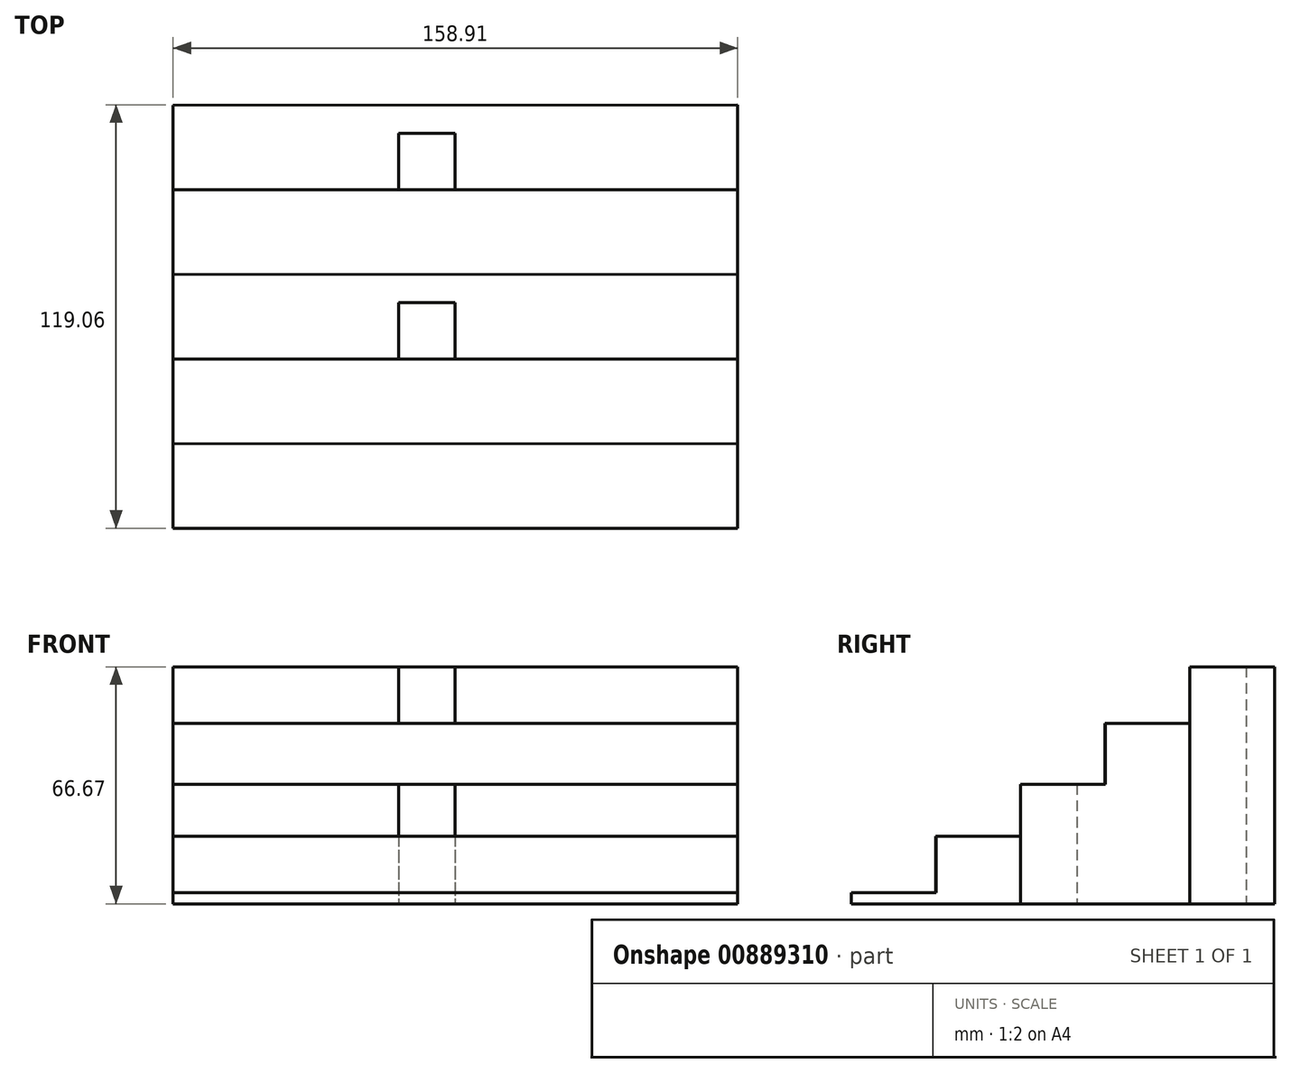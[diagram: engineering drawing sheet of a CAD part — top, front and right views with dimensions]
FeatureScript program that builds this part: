
annotation { "Feature Type Name" : "Feature", "Feature Type Description" : "" }
export const myFeature = defineFeature(function(context is Context, id is Id, definition is map)
    precondition{}
    {
        {
            var Q0;
            Q0=qCreatedBy(makeId("Top.planeOp"),FACE);
            var sketch = newSketch(context, id + "F0", { "sketchPlane" : qUnion([Q0])});
            skLineSegment(sketch, "E0", {"start": v(0, 0) * mm, "end": v(15.88, 0) * mm});
            skLineSegment(sketch, "E1", {"start": v(15.88, 0) * mm, "end": v(15.88, 15.88) * mm});
            skLineSegment(sketch, "E2", {"start": v(15.88, 15.88) * mm, "end": v(0, 15.88) * mm});
            skLineSegment(sketch, "E3", {"start": v(0, 15.88) * mm, "end": v(0, 0) * mm});
            skLineSegment(sketch, "E4.1.0.0", {"start": v(31.75, 0) * mm, "end": v(47.62, 0) * mm});
            skLineSegment(sketch, "E4.1.0.1", {"start": v(31.75, 15.88) * mm, "end": v(31.75, 0) * mm});
            skLineSegment(sketch, "E4.1.0.2", {"start": v(47.62, 0) * mm, "end": v(47.62, 15.88) * mm});
            skLineSegment(sketch, "E4.1.0.3", {"start": v(47.62, 15.88) * mm, "end": v(31.75, 15.88) * mm});
            skLineSegment(sketch, "E4.2.0.0", {"start": v(63.5, 0) * mm, "end": v(79.38, 0) * mm});
            skLineSegment(sketch, "E4.2.0.1", {"start": v(63.5, 15.88) * mm, "end": v(63.5, 0) * mm});
            skLineSegment(sketch, "E4.2.0.2", {"start": v(79.38, 0) * mm, "end": v(79.38, 15.88) * mm});
            skLineSegment(sketch, "E4.2.0.3", {"start": v(79.38, 15.88) * mm, "end": v(63.5, 15.88) * mm});
            skLineSegment(sketch, "E4.3.0.0", {"start": v(95.25, 0) * mm, "end": v(111.12, 0) * mm});
            skLineSegment(sketch, "E4.3.0.1", {"start": v(95.25, 15.88) * mm, "end": v(95.25, 0) * mm});
            skLineSegment(sketch, "E4.3.0.2", {"start": v(111.12, 0) * mm, "end": v(111.12, 15.88) * mm});
            skLineSegment(sketch, "E4.3.0.3", {"start": v(111.12, 15.88) * mm, "end": v(95.25, 15.88) * mm});
            skLineSegment(sketch, "E4.4.0.0", {"start": v(127, 0) * mm, "end": v(142.88, 0) * mm});
            skLineSegment(sketch, "E4.4.0.1", {"start": v(127, 15.88) * mm, "end": v(127, 0) * mm});
            skLineSegment(sketch, "E4.4.0.2", {"start": v(142.88, 0) * mm, "end": v(142.88, 15.88) * mm});
            skLineSegment(sketch, "E4.4.0.3", {"start": v(142.88, 15.88) * mm, "end": v(127, 15.88) * mm});
            skLineSegment(sketch, "E4.direction1", {"start": v(0, 0) * mm, "end": v(31.75, 0) * mm, "construction": true});
            skLineSegment(sketch, "E5.direction1", {"start": v(0, 0) * mm, "end": v(25.4, 0) * mm, "construction": true});
            skLineSegment(sketch, "E5.direction2", {"start": v(0, 0) * mm, "end": v(0, 0) * mm});
            skLineSegment(sketch, "E6.direction1", {"start": v(15.88, 0) * mm, "end": v(31.75, 0) * mm, "construction": true});
            skLineSegment(sketch, "E7", {"start": v(15.88, 23.81) * mm, "end": v(15.88, 39.69) * mm});
            skLineSegment(sketch, "E8", {"start": v(15.88, 39.69) * mm, "end": v(31.8, 39.69) * mm});
            skLineSegment(sketch, "E9", {"start": v(31.8, 39.69) * mm, "end": v(31.8, 23.81) * mm});
            skLineSegment(sketch, "E10", {"start": v(31.8, 23.81) * mm, "end": v(15.88, 23.81) * mm});
            skLineSegment(sketch, "E11.1.0.0", {"start": v(47.62, 23.81) * mm, "end": v(47.62, 39.69) * mm});
            skLineSegment(sketch, "E11.1.0.1", {"start": v(63.55, 39.69) * mm, "end": v(63.55, 23.81) * mm});
            skLineSegment(sketch, "E11.1.0.2", {"start": v(63.55, 23.81) * mm, "end": v(47.62, 23.81) * mm});
            skLineSegment(sketch, "E11.1.0.3", {"start": v(47.62, 39.69) * mm, "end": v(63.55, 39.69) * mm});
            skLineSegment(sketch, "E11.2.0.0", {"start": v(79.38, 23.81) * mm, "end": v(79.38, 39.69) * mm});
            skLineSegment(sketch, "E11.2.0.1", {"start": v(95.3, 39.69) * mm, "end": v(95.3, 23.81) * mm});
            skLineSegment(sketch, "E11.2.0.2", {"start": v(95.3, 23.81) * mm, "end": v(79.37, 23.81) * mm});
            skLineSegment(sketch, "E11.2.0.3", {"start": v(79.37, 39.69) * mm, "end": v(95.3, 39.69) * mm});
            skLineSegment(sketch, "E11.3.0.0", {"start": v(111.12, 23.81) * mm, "end": v(111.12, 39.69) * mm});
            skLineSegment(sketch, "E11.3.0.1", {"start": v(127.05, 39.69) * mm, "end": v(127.05, 23.81) * mm});
            skLineSegment(sketch, "E11.3.0.2", {"start": v(127.05, 23.81) * mm, "end": v(111.12, 23.81) * mm});
            skLineSegment(sketch, "E11.3.0.3", {"start": v(111.12, 39.69) * mm, "end": v(127.05, 39.69) * mm});
            skLineSegment(sketch, "E11.4.0.0", {"start": v(142.88, 23.81) * mm, "end": v(142.88, 39.69) * mm});
            skLineSegment(sketch, "E11.4.0.1", {"start": v(158.8, 39.69) * mm, "end": v(158.8, 23.81) * mm});
            skLineSegment(sketch, "E11.4.0.2", {"start": v(158.8, 23.81) * mm, "end": v(142.87, 23.81) * mm});
            skLineSegment(sketch, "E11.4.0.3", {"start": v(142.87, 39.69) * mm, "end": v(158.8, 39.69) * mm});
            skLineSegment(sketch, "E11.direction1", {"start": v(15.88, 23.81) * mm, "end": v(47.62, 23.81) * mm, "construction": true});
            skLineSegment(sketch, "E12", {"start": v(158.8, 23.81) * mm, "end": v(158.8, 0) * mm});
            skLineSegment(sketch, "E13", {"start": v(158.8, 0) * mm, "end": v(0, 0) * mm});
            skLineSegment(sketch, "E14", {"start": v(-0.01, 23.74) * mm, "end": v(158.8, 23.81) * mm});
            skLineSegment(sketch, "E15", {"start": v(-0.01, 23.74) * mm, "end": v(0, 0) * mm});
            skLineSegment(sketch, "E16", {"start": v(-0.01, 23.74) * mm, "end": v(-0.02, 47.62) * mm});
            skLineSegment(sketch, "E17", {"start": v(-0.02, 47.62) * mm, "end": v(158.89, 47.62) * mm});
            skLineSegment(sketch, "E18", {"start": v(158.89, 47.62) * mm, "end": v(158.8, 23.81) * mm});
            skLineSegment(sketch, "E19.0.1.0", {"start": v(142.88, 71.44) * mm, "end": v(142.88, 87.31) * mm});
            skLineSegment(sketch, "E19.0.1.1", {"start": v(142.88, 47.63) * mm, "end": v(142.88, 63.5) * mm});
            skLineSegment(sketch, "E19.0.1.2", {"start": v(-0.01, 71.37) * mm, "end": v(158.8, 71.44) * mm});
            skLineSegment(sketch, "E19.0.1.3", {"start": v(79.37, 87.31) * mm, "end": v(95.3, 87.31) * mm});
            skLineSegment(sketch, "E19.0.1.4", {"start": v(158.8, 47.63) * mm, "end": v(0, 47.63) * mm});
            skLineSegment(sketch, "E19.0.1.5", {"start": v(15.88, 63.5) * mm, "end": v(0, 63.5) * mm});
            skLineSegment(sketch, "E19.0.1.6", {"start": v(127, 63.5) * mm, "end": v(127, 47.63) * mm});
            skLineSegment(sketch, "E19.0.1.7", {"start": v(63.5, 47.63) * mm, "end": v(79.38, 47.63) * mm});
            skLineSegment(sketch, "E19.0.1.8", {"start": v(15.88, 47.63) * mm, "end": v(15.88, 63.5) * mm});
            skLineSegment(sketch, "E19.0.1.9", {"start": v(111.12, 63.5) * mm, "end": v(95.25, 63.5) * mm});
            skLineSegment(sketch, "E19.0.1.10", {"start": v(0, 63.5) * mm, "end": v(0, 47.63) * mm});
            skLineSegment(sketch, "E19.0.1.11", {"start": v(15.88, 71.44) * mm, "end": v(15.88, 87.31) * mm});
            skLineSegment(sketch, "E19.0.1.12", {"start": v(158.8, 71.44) * mm, "end": v(142.87, 71.44) * mm});
            skLineSegment(sketch, "E19.0.1.13", {"start": v(-0.01, 71.37) * mm, "end": v(0, 47.63) * mm});
            skLineSegment(sketch, "E19.0.1.14", {"start": v(47.62, 87.31) * mm, "end": v(63.55, 87.31) * mm});
            skLineSegment(sketch, "E19.0.1.15", {"start": v(47.62, 71.44) * mm, "end": v(47.62, 87.31) * mm});
            skLineSegment(sketch, "E19.0.1.16", {"start": v(142.87, 87.31) * mm, "end": v(158.8, 87.31) * mm});
            skLineSegment(sketch, "E19.0.1.17", {"start": v(47.62, 47.63) * mm, "end": v(47.62, 63.5) * mm});
            skLineSegment(sketch, "E19.0.1.18", {"start": v(63.55, 87.31) * mm, "end": v(63.55, 71.44) * mm});
            skLineSegment(sketch, "E19.0.1.19", {"start": v(79.38, 63.5) * mm, "end": v(63.5, 63.5) * mm});
            skLineSegment(sketch, "E19.0.1.20", {"start": v(79.38, 71.44) * mm, "end": v(79.38, 87.31) * mm});
            skLineSegment(sketch, "E19.0.1.21", {"start": v(79.38, 47.63) * mm, "end": v(79.38, 63.5) * mm});
            skLineSegment(sketch, "E19.0.1.22", {"start": v(15.88, 87.31) * mm, "end": v(31.8, 87.31) * mm});
            skLineSegment(sketch, "E19.0.1.23", {"start": v(142.88, 63.5) * mm, "end": v(127, 63.5) * mm});
            skLineSegment(sketch, "E19.0.1.24", {"start": v(-0.02, 95.25) * mm, "end": v(158.89, 95.25) * mm});
            skLineSegment(sketch, "E19.0.1.25", {"start": v(95.25, 47.63) * mm, "end": v(111.12, 47.63) * mm});
            skLineSegment(sketch, "E19.0.1.26", {"start": v(31.75, 63.5) * mm, "end": v(31.75, 47.63) * mm});
            skLineSegment(sketch, "E19.0.1.27", {"start": v(111.12, 87.31) * mm, "end": v(127.05, 87.31) * mm});
            skLineSegment(sketch, "E19.0.1.28", {"start": v(127, 47.63) * mm, "end": v(142.88, 47.63) * mm});
            skLineSegment(sketch, "E19.0.1.29", {"start": v(63.5, 63.5) * mm, "end": v(63.5, 47.63) * mm});
            skLineSegment(sketch, "E19.0.1.30", {"start": v(95.25, 63.5) * mm, "end": v(95.25, 47.63) * mm});
            skLineSegment(sketch, "E19.0.1.31", {"start": v(127.05, 71.44) * mm, "end": v(111.12, 71.44) * mm});
            skLineSegment(sketch, "E19.0.1.32", {"start": v(63.55, 71.44) * mm, "end": v(47.62, 71.44) * mm});
            skLineSegment(sketch, "E19.0.1.33", {"start": v(47.62, 63.5) * mm, "end": v(31.75, 63.5) * mm});
            skLineSegment(sketch, "E19.0.1.34", {"start": v(111.12, 71.44) * mm, "end": v(111.12, 87.31) * mm});
            skLineSegment(sketch, "E19.0.1.35", {"start": v(95.3, 71.44) * mm, "end": v(79.37, 71.44) * mm});
            skLineSegment(sketch, "E19.0.1.36", {"start": v(31.8, 87.31) * mm, "end": v(31.8, 71.44) * mm});
            skLineSegment(sketch, "E19.0.1.37", {"start": v(111.12, 47.63) * mm, "end": v(111.12, 63.5) * mm});
            skLineSegment(sketch, "E19.0.1.38", {"start": v(31.8, 71.44) * mm, "end": v(15.88, 71.44) * mm});
            skLineSegment(sketch, "E19.0.1.39", {"start": v(127.05, 87.31) * mm, "end": v(127.05, 71.44) * mm});
            skLineSegment(sketch, "E19.0.1.40", {"start": v(-0.01, 71.37) * mm, "end": v(-0.02, 95.25) * mm});
            skLineSegment(sketch, "E19.0.1.41", {"start": v(95.3, 87.31) * mm, "end": v(95.3, 71.44) * mm});
            skLineSegment(sketch, "E19.0.1.42", {"start": v(158.89, 95.25) * mm, "end": v(158.8, 71.44) * mm});
            skLineSegment(sketch, "E19.0.1.43", {"start": v(158.8, 71.44) * mm, "end": v(158.8, 47.63) * mm});
            skLineSegment(sketch, "E19.0.1.44", {"start": v(0, 47.63) * mm, "end": v(15.88, 47.63) * mm});
            skLineSegment(sketch, "E19.0.1.45", {"start": v(15.88, 71.44) * mm, "end": v(47.62, 71.44) * mm, "construction": true});
            skLineSegment(sketch, "E19.0.1.46", {"start": v(0, 47.63) * mm, "end": v(25.4, 47.63) * mm, "construction": true});
            skLineSegment(sketch, "E19.0.1.47", {"start": v(0, 47.63) * mm, "end": v(31.75, 47.63) * mm, "construction": true});
            skLineSegment(sketch, "E19.0.1.48", {"start": v(158.8, 87.31) * mm, "end": v(158.8, 71.44) * mm});
            skLineSegment(sketch, "E19.0.1.49", {"start": v(31.75, 47.63) * mm, "end": v(47.62, 47.63) * mm});
            skLineSegment(sketch, "E19.0.1.50", {"start": v(15.88, 47.63) * mm, "end": v(31.75, 47.63) * mm, "construction": true});
            skLineSegment(sketch, "E19.direction2", {"start": v(0, 0) * mm, "end": v(0, 47.63) * mm, "construction": true});
            skLineSegment(sketch, "E20.3.0.2", {"start": v(142.88, 95.25) * mm, "end": v(142.88, 111.12) * mm});
            skLineSegment(sketch, "E20.6.0.2", {"start": v(-0.01, 119) * mm, "end": v(158.8, 119.06) * mm});
            skLineSegment(sketch, "E20.12.0.2", {"start": v(158.8, 95.25) * mm, "end": v(0, 95.25) * mm});
            skLineSegment(sketch, "E20.15.0.2", {"start": v(15.88, 111.12) * mm, "end": v(0, 111.12) * mm});
            skLineSegment(sketch, "E20.18.0.2", {"start": v(127, 111.12) * mm, "end": v(127, 95.25) * mm});
            skLineSegment(sketch, "E20.21.0.2", {"start": v(63.5, 95.25) * mm, "end": v(79.38, 95.25) * mm});
            skLineSegment(sketch, "E20.24.0.2", {"start": v(15.88, 95.25) * mm, "end": v(15.88, 111.12) * mm});
            skLineSegment(sketch, "E20.27.0.2", {"start": v(111.12, 111.12) * mm, "end": v(95.25, 111.12) * mm});
            skLineSegment(sketch, "E20.30.0.2", {"start": v(0, 111.12) * mm, "end": v(0, 95.25) * mm});
            skLineSegment(sketch, "E20.39.0.2", {"start": v(-0.01, 119) * mm, "end": v(0, 95.25) * mm});
            skLineSegment(sketch, "E20.51.0.2", {"start": v(47.62, 95.25) * mm, "end": v(47.62, 111.12) * mm});
            skLineSegment(sketch, "E20.57.0.2", {"start": v(79.38, 111.12) * mm, "end": v(63.5, 111.12) * mm});
            skLineSegment(sketch, "E20.63.0.2", {"start": v(79.38, 95.25) * mm, "end": v(79.38, 111.12) * mm});
            skLineSegment(sketch, "E20.69.0.2", {"start": v(142.88, 111.12) * mm, "end": v(127, 111.12) * mm});
            skLineSegment(sketch, "E20.75.0.2", {"start": v(95.25, 95.25) * mm, "end": v(111.12, 95.25) * mm});
            skLineSegment(sketch, "E20.78.0.2", {"start": v(31.75, 111.12) * mm, "end": v(31.75, 95.25) * mm});
            skLineSegment(sketch, "E20.84.0.2", {"start": v(127, 95.25) * mm, "end": v(142.88, 95.25) * mm});
            skLineSegment(sketch, "E20.87.0.2", {"start": v(63.5, 111.12) * mm, "end": v(63.5, 95.25) * mm});
            skLineSegment(sketch, "E20.90.0.2", {"start": v(95.25, 111.12) * mm, "end": v(95.25, 95.25) * mm});
            skLineSegment(sketch, "E20.99.0.2", {"start": v(47.62, 111.12) * mm, "end": v(31.75, 111.12) * mm});
            skLineSegment(sketch, "E20.111.0.2", {"start": v(111.12, 95.25) * mm, "end": v(111.12, 111.12) * mm});
            skLineSegment(sketch, "E20.129.0.2", {"start": v(158.8, 119.06) * mm, "end": v(158.8, 95.25) * mm});
            skLineSegment(sketch, "E20.132.0.2", {"start": v(0, 95.25) * mm, "end": v(15.88, 95.25) * mm});
            skLineSegment(sketch, "E20.138.0.2", {"start": v(0, 95.25) * mm, "end": v(25.4, 95.25) * mm, "construction": true});
            skLineSegment(sketch, "E20.141.0.2", {"start": v(0, 95.25) * mm, "end": v(31.75, 95.25) * mm, "construction": true});
            skLineSegment(sketch, "E20.147.0.2", {"start": v(31.75, 95.25) * mm, "end": v(47.62, 95.25) * mm});
            skLineSegment(sketch, "E20.150.0.2", {"start": v(15.88, 95.25) * mm, "end": v(31.75, 95.25) * mm, "construction": true});
            skSolve(sketch);
        }
        {
            var Q0;
            {var subQ1=sQuery(id+"F0.wireOp",EDGE,"E1");Q0=makeQuery(id+"F0.imprint","IMPRINT",FACE,{"disambiguationData":[TD([[makeQuery(id+"F0.imprint","IMPRINT",EDGE,{"derivedFrom":subQ1}),-1.0]])]});}
            var Q1;
            {var subQ0=sQuery(id+"F0.wireOp",EDGE,"E1");Q1=makeQuery(id+"F0.imprint","IMPRINT",FACE,{"disambiguationData":[TD([[makeQuery(id+"F0.imprint","IMPRINT",EDGE,{"derivedFrom":subQ0}),1.0]])]});}
            var Q2;
            {var subQ0=sQuery(id+"F0.wireOp",EDGE,"E4.1.0.1");Q2=makeQuery(id+"F0.imprint","IMPRINT",FACE,{"disambiguationData":[TD([[makeQuery(id+"F0.imprint","IMPRINT",EDGE,{"derivedFrom":subQ0}),1.0]])]});}
            var Q3;
            {var subQ0=sQuery(id+"F0.wireOp",EDGE,"E4.2.0.1");Q3=makeQuery(id+"F0.imprint","IMPRINT",FACE,{"disambiguationData":[TD([[makeQuery(id+"F0.imprint","IMPRINT",EDGE,{"derivedFrom":subQ0}),1.0]])]});}
            var Q4;
            {var subQ0=sQuery(id+"F0.wireOp",EDGE,"E4.3.0.1");Q4=makeQuery(id+"F0.imprint","IMPRINT",FACE,{"disambiguationData":[TD([[makeQuery(id+"F0.imprint","IMPRINT",EDGE,{"derivedFrom":subQ0}),1.0]])]});}
            var Q5;
            {var subQ0=sQuery(id+"F0.wireOp",EDGE,"E4.4.0.1");Q5=makeQuery(id+"F0.imprint","IMPRINT",FACE,{"disambiguationData":[TD([[makeQuery(id+"F0.imprint","IMPRINT",EDGE,{"derivedFrom":subQ0}),1.0]])]});}
            extrude(context, id + "F1", {"entities" : qUnion([Q0, Q1, Q2, Q3, Q4, Q5]), "depth" : 3.17 * mm, "offsetDistance" : 25.4 * mm});
        }
        {
            var Q0;
            Q0=makeQuery(id+"F0.imprint","IMPRINT",FACE,{"disambiguationData":[TD([[makeQuery(id+"F0.imprint","IMPRINT",EDGE,{"derivedFrom":sQuery(id+"F0.wireOp",EDGE,"E7")}),1.0]])]});
            var Q1;
            Q1=makeQuery(id+"F0.imprint","IMPRINT",FACE,{"disambiguationData":[TD([[makeQuery(id+"F0.imprint","IMPRINT",EDGE,{"derivedFrom":sQuery(id+"F0.wireOp",EDGE,"E7")}),-1.0]])]});
            var Q2;
            Q2=makeQuery(id+"F0.imprint","IMPRINT",FACE,{"disambiguationData":[TD([[makeQuery(id+"F0.imprint","IMPRINT",EDGE,{"derivedFrom":sQuery(id+"F0.wireOp",EDGE,"E11.1.0.0")}),-1.0]])]});
            var Q3;
            Q3=makeQuery(id+"F0.imprint","IMPRINT",FACE,{"disambiguationData":[TD([[makeQuery(id+"F0.imprint","IMPRINT",EDGE,{"derivedFrom":sQuery(id+"F0.wireOp",EDGE,"E11.2.0.0")}),-1.0]])]});
            var Q4;
            Q4=makeQuery(id+"F0.imprint","IMPRINT",FACE,{"disambiguationData":[TD([[makeQuery(id+"F0.imprint","IMPRINT",EDGE,{"derivedFrom":sQuery(id+"F0.wireOp",EDGE,"E11.3.0.0")}),-1.0]])]});
            var Q5;
            Q5=makeQuery(id+"F0.imprint","IMPRINT",FACE,{"disambiguationData":[TD([[makeQuery(id+"F0.imprint","IMPRINT",EDGE,{"derivedFrom":sQuery(id+"F0.wireOp",EDGE,"E11.4.0.0")}),-1.0]])]});
            extrude(context, id + "F2", {"entities" : qUnion([Q0, Q1, Q2, Q3, Q4, Q5]), "operationType" : NewBodyOperationType.ADD, "depth" : 19.05 * mm, "offsetDistance" : 25.4 * mm});
        }
        {
            var Q0;
            {var subQ10=sQuery(id+"F0.wireOp",EDGE,"E19.0.1.1");Q0=makeQuery(id+"F0.imprint","IMPRINT",FACE,{"disambiguationData":[TD([[makeQuery(id+"F0.imprint","IMPRINT",EDGE,{"derivedFrom":subQ10}),-1.0]])]});}
            var Q1;
            Q1=makeQuery(id+"F0.imprint","IMPRINT",FACE,{"disambiguationData":[TD([[makeQuery(id+"F0.imprint","IMPRINT",EDGE,{"derivedFrom":sQuery(id+"F0.wireOp",EDGE,"E19.0.1.5")}),1.0]])]});
            var Q2;
            Q2=makeQuery(id+"F0.imprint","IMPRINT",FACE,{"disambiguationData":[TD([[makeQuery(id+"F0.imprint","IMPRINT",EDGE,{"derivedFrom":sQuery(id+"F0.wireOp",EDGE,"E19.0.1.17")}),1.0]])]});
            var Q3;
            Q3=makeQuery(id+"F0.imprint","IMPRINT",FACE,{"disambiguationData":[TD([[makeQuery(id+"F0.imprint","IMPRINT",EDGE,{"derivedFrom":sQuery(id+"F0.wireOp",EDGE,"E19.0.1.7")}),1.0]])]});
            var Q4;
            Q4=makeQuery(id+"F0.imprint","IMPRINT",FACE,{"disambiguationData":[TD([[makeQuery(id+"F0.imprint","IMPRINT",EDGE,{"derivedFrom":sQuery(id+"F0.wireOp",EDGE,"E19.0.1.9")}),1.0]])]});
            var Q5;
            Q5=makeQuery(id+"F0.imprint","IMPRINT",FACE,{"disambiguationData":[TD([[makeQuery(id+"F0.imprint","IMPRINT",EDGE,{"derivedFrom":sQuery(id+"F0.wireOp",EDGE,"E19.0.1.1")}),1.0]])]});
            extrude(context, id + "F3", {"entities" : qUnion([Q0, Q1, Q2, Q3, Q4, Q5]), "operationType" : NewBodyOperationType.ADD, "depth" : 33.65 * mm, "offsetDistance" : 25.4 * mm});
        }
        {
            var Q0;
            Q0=makeQuery(id+"F0.imprint","IMPRINT",FACE,{"disambiguationData":[TD([[makeQuery(id+"F0.imprint","IMPRINT",EDGE,{"derivedFrom":sQuery(id+"F0.wireOp",EDGE,"E19.0.1.0")}),1.0]])]});
            var Q1;
            Q1=makeQuery(id+"F0.imprint","IMPRINT",FACE,{"disambiguationData":[TD([[makeQuery(id+"F0.imprint","IMPRINT",EDGE,{"derivedFrom":sQuery(id+"F0.wireOp",EDGE,"E19.0.1.11")}),-1.0]])]});
            var Q2;
            Q2=makeQuery(id+"F0.imprint","IMPRINT",FACE,{"disambiguationData":[TD([[makeQuery(id+"F0.imprint","IMPRINT",EDGE,{"derivedFrom":sQuery(id+"F0.wireOp",EDGE,"E19.0.1.14")}),-1.0]])]});
            var Q3;
            Q3=makeQuery(id+"F0.imprint","IMPRINT",FACE,{"disambiguationData":[TD([[makeQuery(id+"F0.imprint","IMPRINT",EDGE,{"derivedFrom":sQuery(id+"F0.wireOp",EDGE,"E19.0.1.3")}),-1.0]])]});
            var Q4;
            Q4=makeQuery(id+"F0.imprint","IMPRINT",FACE,{"disambiguationData":[TD([[makeQuery(id+"F0.imprint","IMPRINT",EDGE,{"derivedFrom":sQuery(id+"F0.wireOp",EDGE,"E19.0.1.27")}),-1.0]])]});
            var Q5;
            Q5=makeQuery(id+"F0.imprint","IMPRINT",FACE,{"disambiguationData":[TD([[makeQuery(id+"F0.imprint","IMPRINT",EDGE,{"derivedFrom":sQuery(id+"F0.wireOp",EDGE,"E19.0.1.0")}),-1.0]])]});
            extrude(context, id + "F4", {"entities" : qUnion([Q0, Q1, Q2, Q3, Q4, Q5]), "operationType" : NewBodyOperationType.ADD, "depth" : 50.8 * mm, "offsetDistance" : 25.4 * mm});
        }
        {
            var Q0;
            Q0=makeQuery(id+"F0.imprint","IMPRINT",FACE,{"disambiguationData":[TD([[makeQuery(id+"F0.imprint","IMPRINT",EDGE,{"derivedFrom":sQuery(id+"F0.wireOp",EDGE,"E20.15.0.2")}),1.0]])]});
            var Q1;
            {var subQ11=sQuery(id+"F0.wireOp",EDGE,"E20.3.0.2");Q1=makeQuery(id+"F0.imprint","IMPRINT",FACE,{"disambiguationData":[TD([[makeQuery(id+"F0.imprint","IMPRINT",EDGE,{"derivedFrom":subQ11}),-1.0]])]});}
            var Q2;
            Q2=makeQuery(id+"F0.imprint","IMPRINT",FACE,{"disambiguationData":[TD([[makeQuery(id+"F0.imprint","IMPRINT",EDGE,{"derivedFrom":sQuery(id+"F0.wireOp",EDGE,"E20.51.0.2")}),1.0]])]});
            var Q3;
            Q3=makeQuery(id+"F0.imprint","IMPRINT",FACE,{"disambiguationData":[TD([[makeQuery(id+"F0.imprint","IMPRINT",EDGE,{"derivedFrom":sQuery(id+"F0.wireOp",EDGE,"E20.21.0.2")}),1.0]])]});
            var Q4;
            Q4=makeQuery(id+"F0.imprint","IMPRINT",FACE,{"disambiguationData":[TD([[makeQuery(id+"F0.imprint","IMPRINT",EDGE,{"derivedFrom":sQuery(id+"F0.wireOp",EDGE,"E20.27.0.2")}),1.0]])]});
            var Q5;
            Q5=makeQuery(id+"F0.imprint","IMPRINT",FACE,{"disambiguationData":[TD([[makeQuery(id+"F0.imprint","IMPRINT",EDGE,{"derivedFrom":sQuery(id+"F0.wireOp",EDGE,"E20.3.0.2")}),1.0]])]});
            extrude(context, id + "F5", {"entities" : qUnion([Q0, Q1, Q2, Q3, Q4, Q5]), "operationType" : NewBodyOperationType.ADD, "depth" : 66.67 * mm, "offsetDistance" : 25.4 * mm});
        }
    });
